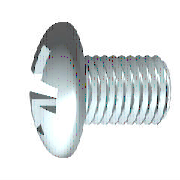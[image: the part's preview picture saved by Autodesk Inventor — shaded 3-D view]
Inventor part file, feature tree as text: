
AUTODESK INVENTOR PART (.ipt)
format: ipt  version: 2013 (Build 170138000, 138)  size: 270,848 bytes
history: native  units: mm (DEFAULTED — no unit token found)
features: extrude x1, other x1, plane x1
ambient origin geometry x7: Origin, YZ Plane, XZ Plane, X Axis, Y Axis, Z Axis, Center Point
bodies: Solid1 (feature_tree), Body (feature_tree)
feature tree (3):
  extrude  "Slot"  Depth=12.7mm
  other  "Cut"
  plane  "Work Plane3"
